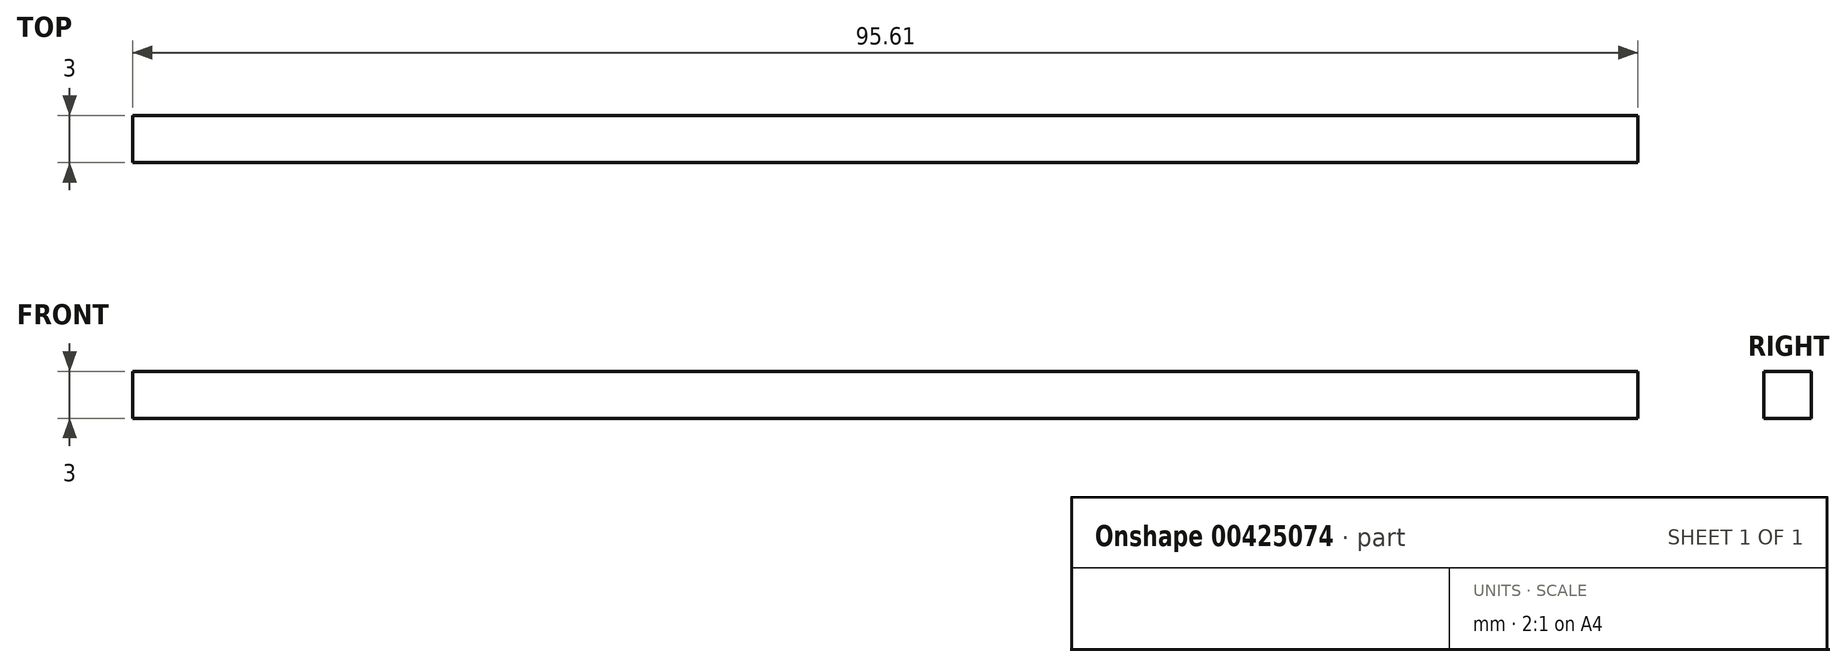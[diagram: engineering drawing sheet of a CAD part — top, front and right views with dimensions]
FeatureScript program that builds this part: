
annotation { "Feature Type Name" : "Feature", "Feature Type Description" : "" }
export const myFeature = defineFeature(function(context is Context, id is Id, definition is map)
    precondition{}
    {
        {
            var Q0;
            Q0=qCreatedBy(makeId("Top.planeOp"),FACE);
            var sketch = newSketch(context, id + "F0", { "sketchPlane" : qUnion([Q0])});
            skLineSegment(sketch, "E0.bottom", {"start": v(-142.94, 6.34) * mm, "end": v(-47.33, 6.34) * mm});
            skLineSegment(sketch, "E0.top", {"start": v(-142.94, 9.34) * mm, "end": v(-47.33, 9.34) * mm});
            skLineSegment(sketch, "E0.left", {"start": v(-142.94, 6.34) * mm, "end": v(-142.94, 9.34) * mm});
            skLineSegment(sketch, "E0.right", {"start": v(-47.33, 6.34) * mm, "end": v(-47.33, 9.34) * mm});
            skSolve(sketch);
        }
        {
            var Q0;
            Q0 = qSketchRegion(id + "F0", true);
            extrude(context, id + "F1", {"entities" : qUnion([Q0]), "depth" : 3 * mm});
        }
    });
